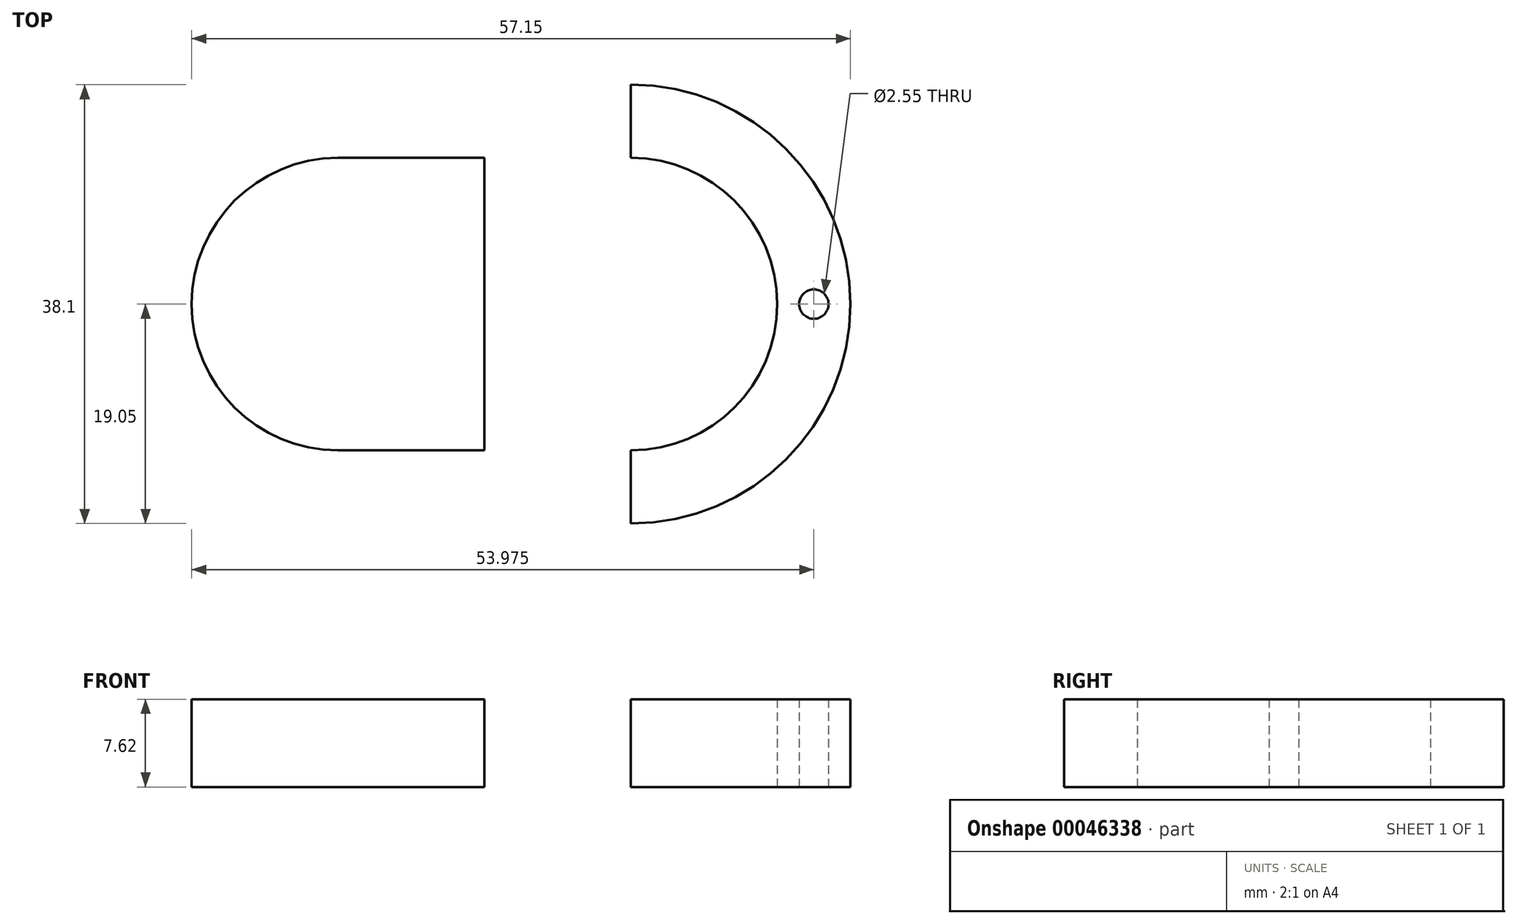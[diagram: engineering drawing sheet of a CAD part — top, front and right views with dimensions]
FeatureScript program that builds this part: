
annotation { "Feature Type Name" : "Feature", "Feature Type Description" : "" }
export const myFeature = defineFeature(function(context is Context, id is Id, definition is map)
    precondition{}
    {
        {
            var Q0;
            Q0=qCreatedBy(makeId("Top.planeOp"),FACE);
            var sketch = newSketch(context, id + "F0", { "sketchPlane" : qUnion([Q0])});
            skLineSegment(sketch, "E0", {"start": v(0, 0) * mm, "end": v(0, 12.7) * mm});
            skLineSegment(sketch, "E1", {"start": v(0, 0) * mm, "end": v(0, -12.7) * mm});
            skLineSegment(sketch, "E2", {"start": v(0, 0) * mm, "end": v(-12.7, 0) * mm});
            skLineSegment(sketch, "E3", {"start": v(0, 0) * mm, "end": v(12.7, 0) * mm});
            skLineSegment(sketch, "E4", {"start": v(0, 12.7) * mm, "end": v(12.7, 12.7) * mm});
            skLineSegment(sketch, "E5", {"start": v(0, 12.7) * mm, "end": v(-12.7, 12.7) * mm});
            skLineSegment(sketch, "E6", {"start": v(0, -12.7) * mm, "end": v(-12.7, -12.7) * mm});
            skLineSegment(sketch, "E7", {"start": v(0, -12.7) * mm, "end": v(12.7, -12.7) * mm});
            skArc(sketch, "E8", {"start": v(12.7, -12.7) * mm, "mid": v(25.4, 0) * mm, "end": v(12.7, 12.7) * mm});
            skArc(sketch, "E9", {"start": v(-12.7, 12.7) * mm, "mid": v(-25.4, 0) * mm, "end": v(-12.7, -12.7) * mm});
            skLineSegment(sketch, "E10", {"start": v(-12.7, 12.7) * mm, "end": v(-12.7, 19.05) * mm});
            skLineSegment(sketch, "E11", {"start": v(12.7, 12.7) * mm, "end": v(12.7, 19.05) * mm});
            skLineSegment(sketch, "E12", {"start": v(-12.7, -12.7) * mm, "end": v(-12.7, -19.05) * mm});
            skLineSegment(sketch, "E13", {"start": v(12.7, -12.7) * mm, "end": v(12.7, -19.05) * mm});
            skArc(sketch, "E14", {"start": v(12.7, -19.05) * mm, "mid": v(31.75, 0) * mm, "end": v(12.7, 19.05) * mm});
            skArc(sketch, "E15", {"start": v(-12.7, 19.05) * mm, "mid": v(-31.75, 0) * mm, "end": v(-12.7, -19.05) * mm});
            skLineSegment(sketch, "E16", {"start": v(-12.7, -19.05) * mm, "end": v(12.7, -19.05) * mm});
            skLineSegment(sketch, "E17", {"start": v(-12.7, 19.05) * mm, "end": v(12.7, 19.05) * mm});
            skCircle(sketch, "E18", {"center": v(12.7, 0) * mm, "radius": 12.7 * mm});
            skLineSegment(sketch, "E19", {"start": v(25.4, 0) * mm, "end": v(28.58, 0) * mm});
            skPoint(sketch, "E19.endSnap0", {"position": v(25.4, 0) * mm});
            skLineSegment(sketch, "E20", {"start": v(0, 12.7) * mm, "end": v(0, 15.88) * mm});
            skLineSegment(sketch, "E21", {"start": v(-25.4, 0) * mm, "end": v(-28.58, 0) * mm});
            skPoint(sketch, "E21.endSnap0", {"position": v(-25.4, 0) * mm});
            skLineSegment(sketch, "E22", {"start": v(0, -12.7) * mm, "end": v(0, -15.88) * mm});
            skCircle(sketch, "E23", {"center": v(-28.58, 0) * mm, "radius": 1.23 * mm});
            skCircle(sketch, "E24", {"center": v(0, 15.88) * mm, "radius": 1.37 * mm});
            skCircle(sketch, "E25", {"center": v(28.58, 0) * mm, "radius": 1.27 * mm});
            skCircle(sketch, "E26", {"center": v(0, -15.88) * mm, "radius": 1.28 * mm});
            skSolve(sketch);
        }
        {
            var Q0;
            Q0=makeQuery(id+"F0.imprint","IMPRINT",FACE,{"disambiguationData":[TD([[makeQuery(id+"F0.imprint","IMPRINT",EDGE,{"derivedFrom":sQuery(id+"F0.wireOp",EDGE,"E0")}),1.0]])]});
            var Q1;
            {var subQ1=sQuery(id+"F0.wireOp",EDGE,"E11");Q1=makeQuery(id+"F0.imprint","IMPRINT",FACE,{"disambiguationData":[TD([[makeQuery(id+"F0.imprint","IMPRINT",EDGE,{"derivedFrom":subQ1}),-1.0]])]});}
            extrude(context, id + "F1", {"entities" : qUnion([Q0, Q1]), "depth" : 7.62 * mm});
        }
    });
